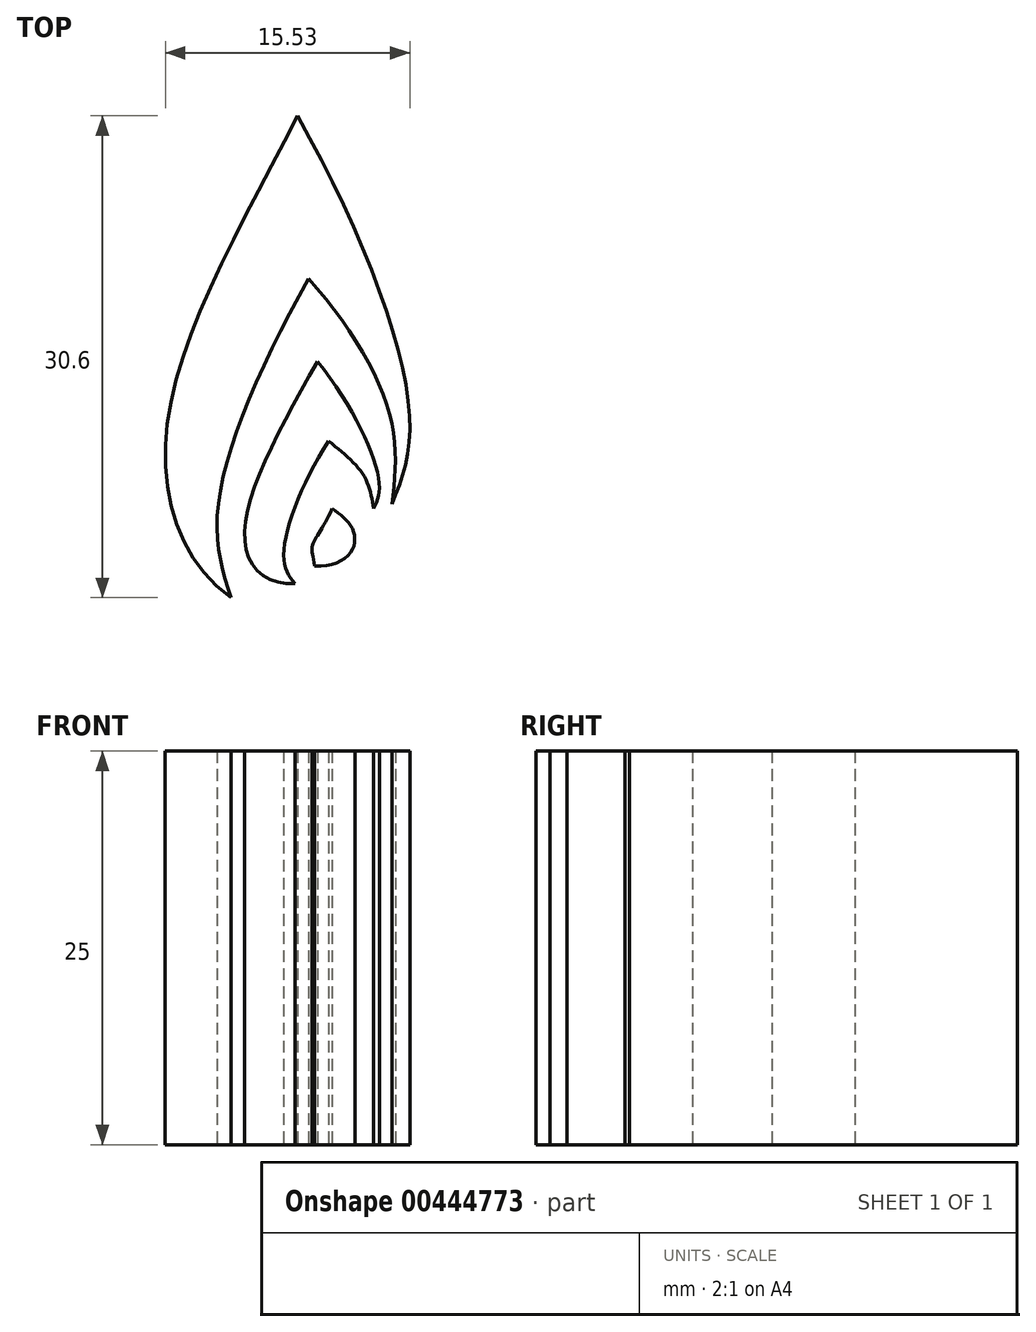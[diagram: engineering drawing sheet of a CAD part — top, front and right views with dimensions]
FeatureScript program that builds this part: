
annotation { "Feature Type Name" : "Feature", "Feature Type Description" : "" }
export const myFeature = defineFeature(function(context is Context, id is Id, definition is map)
    precondition{}
    {
        {
            var Q0;
            Q0=qCreatedBy(makeId("Top.planeOp"),FACE);
            var sketch = newSketch(context, id + "F0", { "sketchPlane" : qUnion([Q0])});
            skFitSpline(sketch, "E0", {"points": [v(-68.6, 50.75) * mm, v(-76.9, 30.7) * mm, v(-72.82, 20.15) * mm], "startDerivative": vector(-18.65, -36.68) * mm, "endDerivative": vector(22.18, -15.78) * mm});
            skFitSpline(sketch, "E1", {"points": [v(-72.82, 20.15) * mm, v(-73.64, 25.88) * mm, v(-67.9, 40.41) * mm], "startDerivative": vector(-4.33, 13.6) * mm, "endDerivative": vector(14.22, 25.4) * mm});
            skFitSpline(sketch, "E2", {"points": [v(-67.9, 40.41) * mm, v(-62.71, 31.71) * mm, v(-62.6, 26.08) * mm], "startDerivative": vector(13.21, -14.77) * mm, "endDerivative": vector(-1.59, -12.74) * mm});
            skFitSpline(sketch, "E3", {"points": [v(-62.6, 26.08) * mm, v(-61.46, 31.63) * mm, v(-68.6, 50.75) * mm], "startDerivative": vector(5.71, 13.83) * mm, "endDerivative": vector(-18.37, 32.07) * mm});
            skFitSpline(sketch, "E4", {"points": [v(-67.33, 35.15) * mm, v(-71.72, 25.8) * mm, v(-71.36, 22.12) * mm, v(-68.75, 21.05) * mm], "startDerivative": vector(-12, -21.3) * mm, "endDerivative": vector(13.09, 1.22) * mm});
            skFitSpline(sketch, "E5", {"points": [v(-68.75, 21.05) * mm, v(-69.46, 22.65) * mm, v(-66.6, 30.08) * mm], "startDerivative": vector(-3.26, 4.08) * mm, "endDerivative": vector(7.54, 11.6) * mm});
            skFitSpline(sketch, "E6", {"points": [v(-66.6, 30.08) * mm, v(-64.4, 27.94) * mm, v(-63.76, 25.8) * mm], "startDerivative": vector(4.8, -3.78) * mm, "endDerivative": vector(0.8, -4.8) * mm});
            skFitSpline(sketch, "E7", {"points": [v(-63.76, 25.8) * mm, v(-63.4, 27.42) * mm, v(-67.33, 35.15) * mm], "startDerivative": vector(2.23, 4.43) * mm, "endDerivative": vector(-9.65, 11.94) * mm});
            skFitSpline(sketch, "E8", {"points": [v(-67.5, 22.15) * mm, v(-67.6, 23.58) * mm, v(-66.4, 25.8) * mm], "startDerivative": vector(-1.05, 5.51) * mm, "endDerivative": vector(2.18, 5.54) * mm});
            skFitSpline(sketch, "E9", {"points": [v(-66.4, 25.8) * mm, v(-65.2, 24.7) * mm, v(-65.09, 23.24) * mm, v(-67.5, 22.15) * mm], "startDerivative": vector(4.46, -3) * mm, "endDerivative": vector(-9.13, 0.57) * mm});
            skSolve(sketch);
        }
        {
            var Q0;
            Q0 = qSketchRegion(id + "F0", true);
            extrude(context, id + "F1", {"entities" : qUnion([Q0]), "depth" : 25 * mm});
        }
    });
